# Revit family: Lighting-Stradale-GEWISS-STREET[O3]-MENSOLA_PARETE
name_source: partatom
category: Apparecchi per illuminazione
units: mm (PartAtom-declared; Revit-internal decimal feet)

## family parameters
Condiviso = No
Host = Superficie
Punto di calcolo locali = No
Quota connettore circolare = Usa diametro
Sorgente d'illuminazione = No
Taglio con vuoti quando caricato = No
Tipo di parte = Normale

## types (1)
- GW86167 - Acciaio zincato - Grigio grafite
    Catalogo = LIGHTING
    Catalogo Serie = STREET [O3]
    Codice EAN = 8011564782518
    Codice Electrocod = 240
    Colore = Grigio grafite
    Descrizione = STREET MENSOLA A PARETE GRIGIO GRAFITE
    Descrizione: = Mensola a parete
    Dim. esterne BxHxP (mm) = 150x160x290
    Dimensioni AxBxC (mm) = 150x160x290
    IDF = 179ceccb-5d67-4ada-ab81-b8eb459a9bc3
    IDT = 734380e8-fd84-4dcf-8fb1-659ccad2240c
    Materiale = Acciaio zincato
    Modello = GW86167
    Peso (kg) = 1,6
    Peso (kg): = 1,6
    Produttore = GEWISS S.p.A.
    Prospetto di default = 1219 mm
    SEO = Mensola
    Scheda Tecnica = https://www.gewiss.com
    URL = https://www.gewiss.com
    Versione file RFA = 19.4
